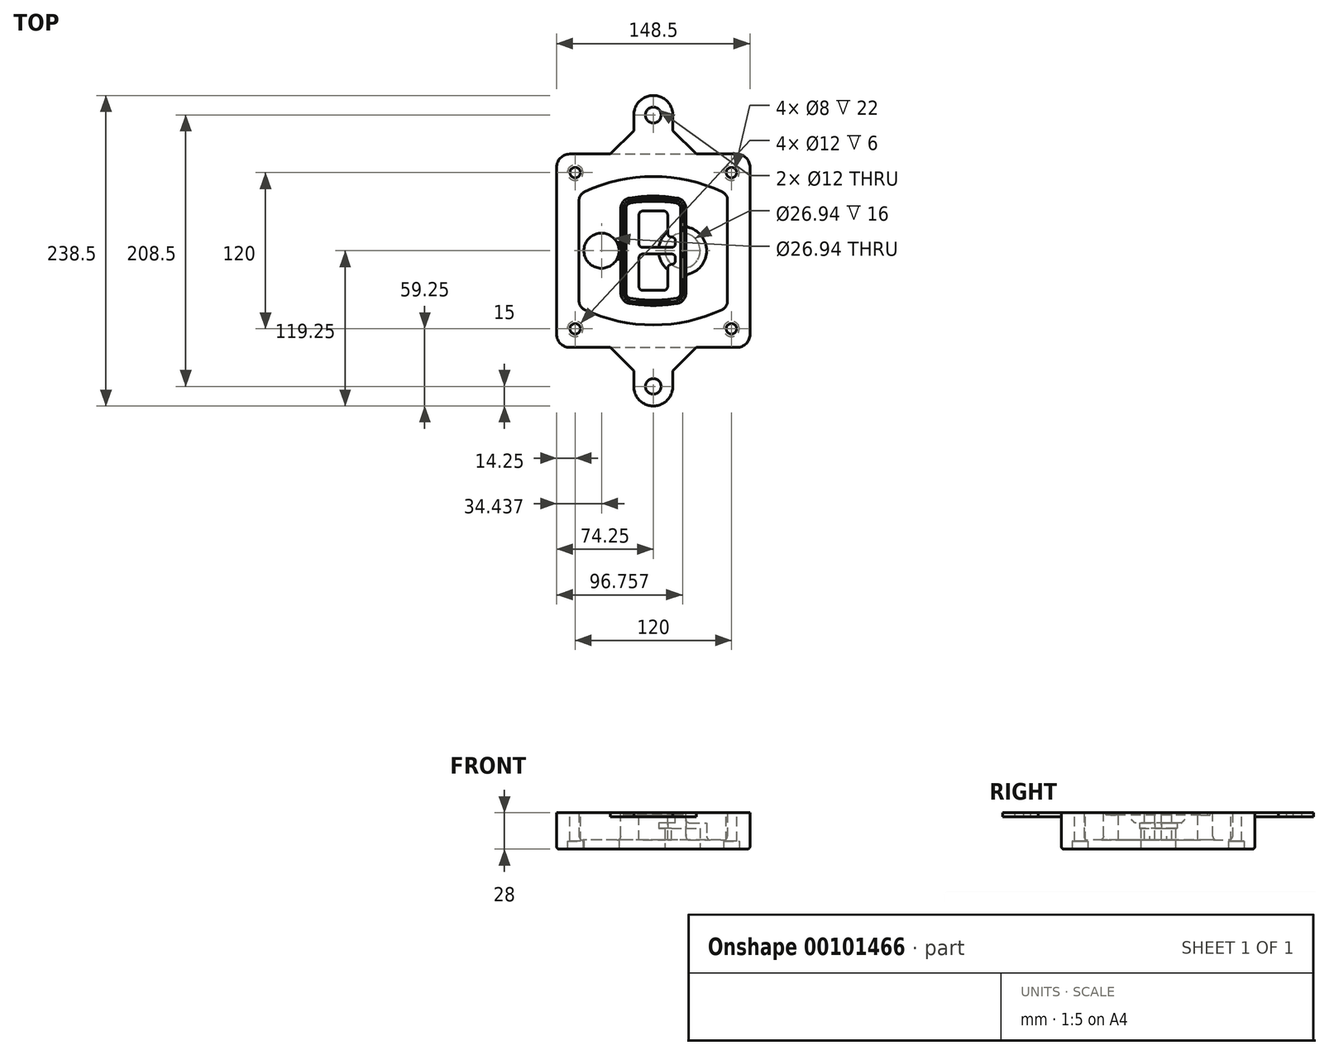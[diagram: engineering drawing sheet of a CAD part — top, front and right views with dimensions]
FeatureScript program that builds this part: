
annotation { "Feature Type Name" : "Feature", "Feature Type Description" : "" }
export const myFeature = defineFeature(function(context is Context, id is Id, definition is map)
    precondition{}
    {
        {
            var Q0;
            Q0=qCreatedBy(makeId("Top.planeOp"),FACE);
            var sketch = newSketch(context, id + "F0", { "sketchPlane" : qUnion([Q0])});
            skPoint(sketch, "E0.rect.middle", {"position": v(0, 0) * mm});
            skLineSegment(sketch, "E1.bottom", {"start": v(-64.25, -74.25) * mm, "end": v(64.25, -74.25) * mm});
            skLineSegment(sketch, "E1.top", {"start": v(-64.25, 74.25) * mm, "end": v(64.25, 74.25) * mm});
            skLineSegment(sketch, "E1.left", {"start": v(-74.25, -64.25) * mm, "end": v(-74.25, 64.25) * mm});
            skLineSegment(sketch, "E1.right", {"start": v(74.25, -64.25) * mm, "end": v(74.25, 64.25) * mm});
            skLineSegment(sketch, "E2", {"start": v(-74.25, 74.25) * mm, "end": v(74.25, -74.25) * mm, "construction": true});
            skLineSegment(sketch, "E3", {"start": v(74.25, 74.25) * mm, "end": v(-74.25, -74.25) * mm, "construction": true});
            skCircle(sketch, "E4", {"center": v(-60, 60) * mm, "radius": 4 * mm});
            skCircle(sketch, "E5", {"center": v(60, 60) * mm, "radius": 4 * mm});
            skCircle(sketch, "E6", {"center": v(60, -60) * mm, "radius": 4 * mm});
            skCircle(sketch, "E7", {"center": v(-60, -60) * mm, "radius": 4 * mm});
            skLineSegment(sketch, "E8", {"start": v(-60, 60) * mm, "end": v(60, 60) * mm, "construction": true});
            skLineSegment(sketch, "E9", {"start": v(60, 60) * mm, "end": v(60, -60) * mm, "construction": true});
            skLineSegment(sketch, "E10", {"start": v(60, -60) * mm, "end": v(-60, -60) * mm, "construction": true});
            skLineSegment(sketch, "E11", {"start": v(-60, -60) * mm, "end": v(-60, 60) * mm, "construction": true});
            skLineSegment(sketch, "E12", {"start": v(-60, 38.83) * mm, "end": v(-60, -38.83) * mm});
            skLineSegment(sketch, "E13", {"start": v(60, 38.83) * mm, "end": v(60, -38.83) * mm});
            skArc(sketch, "E14", {"start": v(54.26, 47.88) * mm, "mid": v(0, 60) * mm, "end": v(-54.26, 47.88) * mm});
            skArc(sketch, "E15", {"start": v(-54.26, -47.88) * mm, "mid": v(0, -60) * mm, "end": v(54.26, -47.88) * mm});
            skLineSegment(sketch, "E16", {"start": v(-60, 0) * mm, "end": v(60, 0) * mm, "construction": true});
            skPoint(sketch, "E17.visualSharp", {"position": v(-60, -45) * mm});
            skArc(sketch, "E17.filletArc", {"start": v(-60, -38.83) * mm, "mid": v(-58.44, -44.2) * mm, "end": v(-54.26, -47.88) * mm});
            skPoint(sketch, "E18.visualSharp", {"position": v(-60, 45) * mm});
            skArc(sketch, "E18.filletArc", {"start": v(-54.26, 47.88) * mm, "mid": v(-58.44, 44.2) * mm, "end": v(-60, 38.83) * mm});
            skPoint(sketch, "E19.visualSharp", {"position": v(60, 45) * mm});
            skArc(sketch, "E19.filletArc", {"start": v(60, 38.83) * mm, "mid": v(58.44, 44.2) * mm, "end": v(54.26, 47.88) * mm});
            skPoint(sketch, "E20.visualSharp", {"position": v(60, -45) * mm});
            skArc(sketch, "E20.filletArc", {"start": v(54.26, -47.88) * mm, "mid": v(58.44, -44.2) * mm, "end": v(60, -38.83) * mm});
            skPoint(sketch, "E21.visualSharp", {"position": v(-74.25, 74.25) * mm});
            skArc(sketch, "E21.filletArc", {"start": v(-64.25, 74.25) * mm, "mid": v(-71.32, 71.32) * mm, "end": v(-74.25, 64.25) * mm});
            skPoint(sketch, "E22.visualSharp", {"position": v(74.25, 74.25) * mm});
            skArc(sketch, "E22.filletArc", {"start": v(74.25, 64.25) * mm, "mid": v(71.32, 71.32) * mm, "end": v(64.25, 74.25) * mm});
            skPoint(sketch, "E23.visualSharp", {"position": v(74.25, -74.25) * mm});
            skArc(sketch, "E23.filletArc", {"start": v(64.25, -74.25) * mm, "mid": v(71.32, -71.32) * mm, "end": v(74.25, -64.25) * mm});
            skPoint(sketch, "E24.visualSharp", {"position": v(-74.25, -74.25) * mm});
            skArc(sketch, "E24.filletArc", {"start": v(-74.25, -64.25) * mm, "mid": v(-71.32, -71.32) * mm, "end": v(-64.25, -74.25) * mm});
            skArc(sketch, "E25.0", {"start": v(57, 38.83) * mm, "mid": v(55.9, 42.58) * mm, "end": v(52.98, 45.17) * mm});
            skLineSegment(sketch, "E25.1", {"start": v(57, 38.83) * mm, "end": v(57, -38.83) * mm});
            skArc(sketch, "E25.2", {"start": v(52.98, -45.17) * mm, "mid": v(55.9, -42.58) * mm, "end": v(57, -38.83) * mm});
            skArc(sketch, "E25.3", {"start": v(-52.98, -45.17) * mm, "mid": v(0, -57) * mm, "end": v(52.98, -45.17) * mm});
            skArc(sketch, "E25.4", {"start": v(-57, -38.83) * mm, "mid": v(-55.9, -42.58) * mm, "end": v(-52.98, -45.17) * mm});
            skArc(sketch, "E25.5", {"start": v(52.98, 45.17) * mm, "mid": v(0, 57) * mm, "end": v(-52.98, 45.17) * mm});
            skLineSegment(sketch, "E25.6", {"start": v(-57, 38.83) * mm, "end": v(-57, -38.83) * mm});
            skArc(sketch, "E25.7", {"start": v(-52.98, 45.17) * mm, "mid": v(-55.9, 42.58) * mm, "end": v(-57, 38.83) * mm});
            skArc(sketch, "E26.0", {"start": v(-55.96, 51.5) * mm, "mid": v(-61.82, 46.33) * mm, "end": v(-64, 38.83) * mm});
            skArc(sketch, "E26.1", {"start": v(55.96, 51.5) * mm, "mid": v(0, 64) * mm, "end": v(-55.96, 51.5) * mm});
            skArc(sketch, "E26.2", {"start": v(64, 38.83) * mm, "mid": v(61.82, 46.33) * mm, "end": v(55.96, 51.5) * mm});
            skLineSegment(sketch, "E26.3", {"start": v(64, 38.83) * mm, "end": v(64, -38.83) * mm});
            skArc(sketch, "E26.4", {"start": v(55.96, -51.5) * mm, "mid": v(61.82, -46.33) * mm, "end": v(64, -38.83) * mm});
            skLineSegment(sketch, "E26.5", {"start": v(-64, 38.83) * mm, "end": v(-64, -38.83) * mm});
            skArc(sketch, "E26.6", {"start": v(-55.96, -51.5) * mm, "mid": v(0, -64) * mm, "end": v(55.96, -51.5) * mm});
            skArc(sketch, "E26.7", {"start": v(-64, -38.83) * mm, "mid": v(-61.82, -46.33) * mm, "end": v(-55.96, -51.5) * mm});
            skSolve(sketch);
        }
        {
            var Q0;
            Q0=makeQuery(id+"F0.imprint","IMPRINT",FACE,{"disambiguationData":[TD([[makeQuery(id+"F0.imprint","IMPRINT",EDGE,{"derivedFrom":sQuery(id+"F0.wireOp",EDGE,"E1.bottom")}),1.0]])]});
            var Q1;
            Q1=makeQuery(id+"F0.imprint","IMPRINT",FACE,{"disambiguationData":[TD([[makeQuery(id+"F0.imprint","IMPRINT",EDGE,{"derivedFrom":sQuery(id+"F0.wireOp",EDGE,"E12")}),1.0]])]});
            var Q2;
            Q2=makeQuery(id+"F0.imprint","IMPRINT",FACE,{"disambiguationData":[TD([[makeQuery(id+"F0.imprint","IMPRINT",EDGE,{"derivedFrom":sQuery(id+"F0.wireOp",EDGE,"E25.0")}),1.0]])]});
            var Q3;
            Q3=makeQuery(id+"F0.imprint","IMPRINT",FACE,{"disambiguationData":[TD([[makeQuery(id+"F0.imprint","IMPRINT",EDGE,{"derivedFrom":sQuery(id+"F0.wireOp",EDGE,"E12")}),-1.0]])]});
            extrude(context, id + "F1", {"entities" : qUnion([Q0, Q1, Q2, Q3]), "oppositeDirection" : true, "depth" : 25 * mm});
        }
        {
            var Q0;
            Q0=makeQuery(id+"F0.imprint","IMPRINT",FACE,{"disambiguationData":[TD([[makeQuery(id+"F0.imprint","IMPRINT",EDGE,{"derivedFrom":sQuery(id+"F0.wireOp",EDGE,"E12")}),1.0]])]});
            extrude(context, id + "F2", {"entities" : qUnion([Q0]), "operationType" : NewBodyOperationType.ADD, "depth" : 3 * mm});
        }
        {
            var Q0;
            Q0=makeQuery(id+"F0.imprint","IMPRINT",FACE,{"disambiguationData":[TD([[makeQuery(id+"F0.imprint","IMPRINT",EDGE,{"derivedFrom":sQuery(id+"F0.wireOp",EDGE,"E25.0")}),1.0]])]});
            extrude(context, id + "F3", {"entities" : qUnion([Q0]), "operationType" : NewBodyOperationType.REMOVE, "oppositeDirection" : true, "depth" : 18 * mm});
        }
        {
            var Q0;
            Q0=makeQuery(id+"F2.opExtrude","CAP_FACE",FACE,{"disambiguationData":[OSD([sQuery(id+"F0.wireOp",EDGE,"E12"),sQuery(id+"F0.wireOp",EDGE,"E13"),sQuery(id+"F0.wireOp",EDGE,"E14"),sQuery(id+"F0.wireOp",EDGE,"E15"),sQuery(id+"F0.wireOp",EDGE,"E17.filletArc"),sQuery(id+"F0.wireOp",EDGE,"E18.filletArc"),sQuery(id+"F0.wireOp",EDGE,"E19.filletArc"),sQuery(id+"F0.wireOp",EDGE,"E20.filletArc"),sQuery(id+"F0.wireOp",EDGE,"E25.0"),sQuery(id+"F0.wireOp",EDGE,"E25.1"),sQuery(id+"F0.wireOp",EDGE,"E25.2"),sQuery(id+"F0.wireOp",EDGE,"E25.3"),sQuery(id+"F0.wireOp",EDGE,"E25.4"),sQuery(id+"F0.wireOp",EDGE,"E25.5"),sQuery(id+"F0.wireOp",EDGE,"E25.6"),sQuery(id+"F0.wireOp",EDGE,"E25.7")])],"isStart":false});
            var sketch = newSketch(context, id + "F4", { "sketchPlane" : qUnion([Q0])});
            skArc(sketch, "E27.0", {"start": v(-18.34, -40.45) * mm, "mid": v(0, -42) * mm, "end": v(18.34, -40.45) * mm});
            skArc(sketch, "E28.0", {"start": v(18.34, 40.45) * mm, "mid": v(0, 42) * mm, "end": v(-18.34, 40.45) * mm});
            skLineSegment(sketch, "E29", {"start": v(-25, 32.57) * mm, "end": v(-25, -32.57) * mm});
            skLineSegment(sketch, "E30", {"start": v(25, 32.57) * mm, "end": v(25, -32.57) * mm});
            skLineSegment(sketch, "E31", {"start": v(-25, 39.1) * mm, "end": v(25, 39.1) * mm, "construction": true});
            skLineSegment(sketch, "E32", {"start": v(-25, -39.1) * mm, "end": v(25, -39.1) * mm, "construction": true});
            skPoint(sketch, "E33.visualSharp", {"position": v(-25, 39.1) * mm});
            skArc(sketch, "E33.filletArc", {"start": v(-18.34, 40.45) * mm, "mid": v(-23.11, 37.73) * mm, "end": v(-25, 32.57) * mm});
            skPoint(sketch, "E34.visualSharp", {"position": v(25, 39.1) * mm});
            skArc(sketch, "E34.filletArc", {"start": v(25, 32.57) * mm, "mid": v(23.11, 37.73) * mm, "end": v(18.34, 40.45) * mm});
            skPoint(sketch, "E35.visualSharp", {"position": v(25, -39.1) * mm});
            skArc(sketch, "E35.filletArc", {"start": v(18.34, -40.45) * mm, "mid": v(23.11, -37.73) * mm, "end": v(25, -32.57) * mm});
            skPoint(sketch, "E36.visualSharp", {"position": v(-25, -39.1) * mm});
            skArc(sketch, "E36.filletArc", {"start": v(-25, -32.57) * mm, "mid": v(-23.11, -37.73) * mm, "end": v(-18.34, -40.45) * mm});
            skArc(sketch, "E37.0", {"start": v(52.98, 45.17) * mm, "mid": v(0, 57) * mm, "end": v(-52.98, 45.17) * mm});
            skArc(sketch, "E37.1", {"start": v(-52.98, 45.17) * mm, "mid": v(-55.9, 42.58) * mm, "end": v(-57, 38.83) * mm});
            skLineSegment(sketch, "E37.2", {"start": v(-57, 38.83) * mm, "end": v(-57, -38.83) * mm});
            skArc(sketch, "E37.3", {"start": v(-57, -38.83) * mm, "mid": v(-55.9, -42.58) * mm, "end": v(-52.98, -45.17) * mm});
            skArc(sketch, "E37.4", {"start": v(-52.98, -45.17) * mm, "mid": v(0, -57) * mm, "end": v(52.98, -45.17) * mm});
            skArc(sketch, "E37.5", {"start": v(52.98, -45.17) * mm, "mid": v(55.9, -42.58) * mm, "end": v(57, -38.83) * mm});
            skLineSegment(sketch, "E37.6", {"start": v(57, 38.83) * mm, "end": v(57, -38.83) * mm});
            skArc(sketch, "E37.7", {"start": v(57, 38.83) * mm, "mid": v(55.9, 42.58) * mm, "end": v(52.98, 45.17) * mm});
            skLineSegment(sketch, "E38.0", {"start": v(23, 32.57) * mm, "end": v(23, -32.57) * mm});
            skArc(sketch, "E38.1", {"start": v(18, -38.48) * mm, "mid": v(21.58, -36.44) * mm, "end": v(23, -32.57) * mm});
            skArc(sketch, "E38.2", {"start": v(-18, -38.48) * mm, "mid": v(0, -40) * mm, "end": v(18, -38.48) * mm});
            skArc(sketch, "E38.3", {"start": v(-23, -32.57) * mm, "mid": v(-21.58, -36.44) * mm, "end": v(-18, -38.48) * mm});
            skLineSegment(sketch, "E38.4", {"start": v(-23, 32.57) * mm, "end": v(-23, -32.57) * mm});
            skArc(sketch, "E38.5", {"start": v(23, 32.57) * mm, "mid": v(21.58, 36.44) * mm, "end": v(18, 38.48) * mm});
            skArc(sketch, "E38.6", {"start": v(-18, 38.48) * mm, "mid": v(-21.58, 36.44) * mm, "end": v(-23, 32.57) * mm});
            skArc(sketch, "E38.7", {"start": v(18, 38.48) * mm, "mid": v(0, 40) * mm, "end": v(-18, 38.48) * mm});
            skArc(sketch, "E39.0", {"start": v(21, 32.57) * mm, "mid": v(20.06, 35.15) * mm, "end": v(17.67, 36.5) * mm});
            skLineSegment(sketch, "E39.1", {"start": v(21, 32.57) * mm, "end": v(21, -32.57) * mm});
            skArc(sketch, "E39.2", {"start": v(17.67, -36.5) * mm, "mid": v(20.06, -35.15) * mm, "end": v(21, -32.57) * mm});
            skArc(sketch, "E39.3", {"start": v(-17.67, -36.5) * mm, "mid": v(0, -38) * mm, "end": v(17.67, -36.5) * mm});
            skArc(sketch, "E39.4", {"start": v(-21, -32.57) * mm, "mid": v(-20.06, -35.15) * mm, "end": v(-17.67, -36.5) * mm});
            skArc(sketch, "E39.5", {"start": v(17.67, 36.5) * mm, "mid": v(0, 38) * mm, "end": v(-17.67, 36.5) * mm});
            skLineSegment(sketch, "E39.6", {"start": v(-21, 32.57) * mm, "end": v(-21, -32.57) * mm});
            skArc(sketch, "E39.7", {"start": v(-17.67, 36.5) * mm, "mid": v(-20.06, 35.15) * mm, "end": v(-21, 32.57) * mm});
            skLineSegment(sketch, "E40", {"start": v(-25, 0) * mm, "end": v(25, 0) * mm, "construction": true});
            skLineSegment(sketch, "E41", {"start": v(-11, 5.5) * mm, "end": v(-11, 27.5) * mm});
            skLineSegment(sketch, "E42", {"start": v(-8, 30.5) * mm, "end": v(8, 30.5) * mm});
            skLineSegment(sketch, "E43", {"start": v(11, 27.5) * mm, "end": v(11, 13.5) * mm});
            skLineSegment(sketch, "E44", {"start": v(14, 10.5) * mm, "end": v(14, 10.5) * mm});
            skLineSegment(sketch, "E45", {"start": v(17, 7.5) * mm, "end": v(17, 5.5) * mm});
            skLineSegment(sketch, "E46", {"start": v(14, 2.5) * mm, "end": v(-8, 2.5) * mm});
            skPoint(sketch, "E47.visualSharp", {"position": v(-11, 30.5) * mm});
            skArc(sketch, "E47.filletArc", {"start": v(-8, 30.5) * mm, "mid": v(-10.12, 29.62) * mm, "end": v(-11, 27.5) * mm});
            skPoint(sketch, "E48.visualSharp", {"position": v(11, 30.5) * mm});
            skArc(sketch, "E48.filletArc", {"start": v(11, 27.5) * mm, "mid": v(10.12, 29.62) * mm, "end": v(8, 30.5) * mm});
            skPoint(sketch, "E49.visualSharp", {"position": v(11, 10.5) * mm});
            skArc(sketch, "E49.filletArc", {"start": v(11, 13.5) * mm, "mid": v(11.88, 11.38) * mm, "end": v(14, 10.5) * mm});
            skPoint(sketch, "E50.visualSharp", {"position": v(17, 10.5) * mm});
            skArc(sketch, "E50.filletArc", {"start": v(17, 7.5) * mm, "mid": v(16.12, 9.62) * mm, "end": v(14, 10.5) * mm});
            skPoint(sketch, "E51.visualSharp", {"position": v(17, 2.5) * mm});
            skArc(sketch, "E51.filletArc", {"start": v(14, 2.5) * mm, "mid": v(16.12, 3.38) * mm, "end": v(17, 5.5) * mm});
            skPoint(sketch, "E52.visualSharp", {"position": v(-11, 2.5) * mm});
            skArc(sketch, "E52.filletArc", {"start": v(-11, 5.5) * mm, "mid": v(-10.12, 3.38) * mm, "end": v(-8, 2.5) * mm});
            skLineSegment(sketch, "E53.0.MirrorCS", {"start": v(14, -2.5) * mm, "end": v(-8, -2.5) * mm});
            skArc(sketch, "E54.0.MirrorCS", {"start": v(-11, -5.5) * mm, "mid": v(-10.12, -3.38) * mm, "end": v(-8, -2.5) * mm});
            skLineSegment(sketch, "E55.0.MirrorCS", {"start": v(-11, -5.5) * mm, "end": v(-11, -27.5) * mm});
            skArc(sketch, "E56.0.MirrorCS", {"start": v(-8, -30.5) * mm, "mid": v(-10.12, -29.62) * mm, "end": v(-11, -27.5) * mm});
            skLineSegment(sketch, "E57.0.MirrorCS", {"start": v(-8, -30.5) * mm, "end": v(8, -30.5) * mm});
            skArc(sketch, "E58.0.MirrorCS", {"start": v(11, -27.5) * mm, "mid": v(10.12, -29.62) * mm, "end": v(8, -30.5) * mm});
            skLineSegment(sketch, "E59.0.MirrorCS", {"start": v(11, -27.5) * mm, "end": v(11, -13.5) * mm});
            skArc(sketch, "E60.0.MirrorCS", {"start": v(11, -13.5) * mm, "mid": v(11.88, -11.38) * mm, "end": v(14, -10.5) * mm});
            skArc(sketch, "E61.0.MirrorCS", {"start": v(17, -7.5) * mm, "mid": v(16.12, -9.62) * mm, "end": v(14, -10.5) * mm});
            skLineSegment(sketch, "E62.0.MirrorCS", {"start": v(17, -7.5) * mm, "end": v(17, -5.5) * mm});
            skArc(sketch, "E63.0.MirrorCS", {"start": v(14, -2.5) * mm, "mid": v(16.12, -3.38) * mm, "end": v(17, -5.5) * mm});
            skSolve(sketch);
        }
        {
            var Q0;
            Q0=makeQuery(id+"F4.imprint","IMPRINT",FACE,{"disambiguationData":[TD([[makeQuery(id+"F4.imprint","IMPRINT",EDGE,{"derivedFrom":sQuery(id+"F4.wireOp",EDGE,"E27.0")}),1.0]])]});
            var Q1;
            Q1=makeQuery(id+"F4.imprint","IMPRINT",FACE,{"disambiguationData":[TD([[makeQuery(id+"F4.imprint","IMPRINT",EDGE,{"derivedFrom":sQuery(id+"F4.wireOp",EDGE,"E38.0")}),-1.0]])]});
            var Q2;
            Q2=makeQuery(id+"F4.imprint","IMPRINT",FACE,{"disambiguationData":[TD([[makeQuery(id+"F4.imprint","IMPRINT",EDGE,{"derivedFrom":sQuery(id+"F4.wireOp",EDGE,"E39.0")}),1.0]])]});
            extrude(context, id + "F5", {"entities" : qUnion([Q0, Q1, Q2]), "operationType" : NewBodyOperationType.ADD, "endBound" : BoundingType.UP_TO_NEXT, "oppositeDirection" : true, "depth" : 25 * mm});
        }
        {
            var Q0;
            Q0=makeQuery(id+"F4.imprint","IMPRINT",FACE,{"disambiguationData":[TD([[makeQuery(id+"F4.imprint","IMPRINT",EDGE,{"derivedFrom":sQuery(id+"F4.wireOp",EDGE,"E38.0")}),-1.0]])]});
            extrude(context, id + "F6", {"entities" : qUnion([Q0]), "operationType" : NewBodyOperationType.REMOVE, "oppositeDirection" : true, "depth" : 2 * mm});
        }
        {
            var Q0;
            Q0=makeQuery(id+"F1.opExtrude","CAP_FACE",FACE,{"disambiguationData":[OSD([sQuery(id+"F0.wireOp",EDGE,"E1.bottom"),sQuery(id+"F0.wireOp",EDGE,"E1.top"),sQuery(id+"F0.wireOp",EDGE,"E1.left"),sQuery(id+"F0.wireOp",EDGE,"E1.right"),sQuery(id+"F0.wireOp",EDGE,"E4"),sQuery(id+"F0.wireOp",EDGE,"E5"),sQuery(id+"F0.wireOp",EDGE,"E6"),sQuery(id+"F0.wireOp",EDGE,"E7"),sQuery(id+"F0.wireOp",EDGE,"E21.filletArc"),sQuery(id+"F0.wireOp",EDGE,"E22.filletArc"),sQuery(id+"F0.wireOp",EDGE,"E23.filletArc"),sQuery(id+"F0.wireOp",EDGE,"E24.filletArc")])],"isStart":false});
            var sketch = newSketch(context, id + "F7", { "sketchPlane" : qUnion([Q0])});
            skCircle(sketch, "E64", {"center": v(22.5, 0) * mm, "radius": 13.47 * mm});
            skCircle(sketch, "E65", {"center": v(-39.81, 0) * mm, "radius": 13.47 * mm});
            skLineSegment(sketch, "E66", {"start": v(74.25, 0) * mm, "end": v(-74.25, 0) * mm});
            skCircle(sketch, "E67", {"center": v(22.5, 0) * mm, "radius": 18.47 * mm});
            skCircle(sketch, "E68", {"center": v(60, -60) * mm, "radius": 6 * mm});
            skCircle(sketch, "E69", {"center": v(-60, -60) * mm, "radius": 6 * mm});
            skCircle(sketch, "E70", {"center": v(-60, 60) * mm, "radius": 6 * mm});
            skCircle(sketch, "E71", {"center": v(60, 60) * mm, "radius": 6 * mm});
            skSolve(sketch);
        }
        {
            var Q0;
            {var subQ1=sQuery(id+"F7.wireOp",EDGE,"E66");var subQ4=sQuery(id+"F7.wireOp",EDGE,"E64");var subQ6=makeQuery(id+"F7.imprint","INTERSECT",VERTEX,{"disambiguationData":[OD(0.0)],"derivedFrom":[subQ4,subQ1]});Q0=makeQuery(id+"F7.imprint","IMPRINT",FACE,{"disambiguationData":[TD([[makeQuery(id+"F7.imprint","IMPRINT",EDGE,{"disambiguationData":[TD([[subQ6,-1.0]])],"derivedFrom":subQ4}),-1.0]])]});}
            var Q1;
            {var subQ0=sQuery(id+"F7.wireOp",EDGE,"E66");var subQ1=sQuery(id+"F7.wireOp",EDGE,"E64");var subQ3=makeQuery(id+"F7.imprint","INTERSECT",VERTEX,{"disambiguationData":[OD(0.0)],"derivedFrom":[subQ1,subQ0]});Q1=makeQuery(id+"F7.imprint","IMPRINT",FACE,{"disambiguationData":[TD([[makeQuery(id+"F7.imprint","IMPRINT",EDGE,{"disambiguationData":[TD([[subQ3,-1.0]])],"derivedFrom":subQ1}),1.0]])]});}
            var Q2;
            {var subQ0=sQuery(id+"F7.wireOp",EDGE,"E66");var subQ1=sQuery(id+"F7.wireOp",EDGE,"E64");var subQ3=makeQuery(id+"F7.imprint","INTERSECT",VERTEX,{"disambiguationData":[OD(0.0)],"derivedFrom":[subQ1,subQ0]});Q2=makeQuery(id+"F7.imprint","IMPRINT",FACE,{"disambiguationData":[TD([[makeQuery(id+"F7.imprint","IMPRINT",EDGE,{"disambiguationData":[TD([[subQ3,1.0]])],"derivedFrom":subQ1}),1.0]])]});}
            var Q3;
            {var subQ1=sQuery(id+"F7.wireOp",EDGE,"E66");var subQ4=sQuery(id+"F7.wireOp",EDGE,"E64");var subQ6=makeQuery(id+"F7.imprint","INTERSECT",VERTEX,{"disambiguationData":[OD(0.0)],"derivedFrom":[subQ4,subQ1]});Q3=makeQuery(id+"F7.imprint","IMPRINT",FACE,{"disambiguationData":[TD([[makeQuery(id+"F7.imprint","IMPRINT",EDGE,{"disambiguationData":[TD([[subQ6,1.0]])],"derivedFrom":subQ4}),-1.0]])]});}
            extrude(context, id + "F8", {"entities" : qUnion([Q0, Q1, Q2, Q3]), "operationType" : NewBodyOperationType.ADD, "oppositeDirection" : true, "depth" : 20 * mm});
        }
        {
            var Q0;
            {var subQ0=sQuery(id+"F7.wireOp",EDGE,"E66");var subQ1=sQuery(id+"F7.wireOp",EDGE,"E64");var subQ3=makeQuery(id+"F7.imprint","INTERSECT",VERTEX,{"disambiguationData":[OD(0.0)],"derivedFrom":[subQ1,subQ0]});Q0=makeQuery(id+"F7.imprint","IMPRINT",FACE,{"disambiguationData":[TD([[makeQuery(id+"F7.imprint","IMPRINT",EDGE,{"disambiguationData":[TD([[subQ3,-1.0]])],"derivedFrom":subQ1}),1.0]])]});}
            var Q1;
            {var subQ0=sQuery(id+"F7.wireOp",EDGE,"E66");var subQ1=sQuery(id+"F7.wireOp",EDGE,"E64");var subQ3=makeQuery(id+"F7.imprint","INTERSECT",VERTEX,{"disambiguationData":[OD(0.0)],"derivedFrom":[subQ1,subQ0]});Q1=makeQuery(id+"F7.imprint","IMPRINT",FACE,{"disambiguationData":[TD([[makeQuery(id+"F7.imprint","IMPRINT",EDGE,{"disambiguationData":[TD([[subQ3,1.0]])],"derivedFrom":subQ1}),1.0]])]});}
            extrude(context, id + "F9", {"entities" : qUnion([Q0, Q1]), "operationType" : NewBodyOperationType.REMOVE, "oppositeDirection" : true, "depth" : 16 * mm});
        }
        {
            var Q0;
            {var subQ0=sQuery(id+"F7.wireOp",EDGE,"E66");var subQ1=sQuery(id+"F7.wireOp",EDGE,"E65");var subQ3=makeQuery(id+"F7.imprint","INTERSECT",VERTEX,{"disambiguationData":[OD(0.0)],"derivedFrom":[subQ1,subQ0]});Q0=makeQuery(id+"F7.imprint","IMPRINT",FACE,{"disambiguationData":[TD([[makeQuery(id+"F7.imprint","IMPRINT",EDGE,{"disambiguationData":[TD([[subQ3,-1.0]])],"derivedFrom":subQ1}),1.0]])]});}
            var Q1;
            {var subQ0=sQuery(id+"F7.wireOp",EDGE,"E66");var subQ1=sQuery(id+"F7.wireOp",EDGE,"E65");var subQ3=makeQuery(id+"F7.imprint","INTERSECT",VERTEX,{"disambiguationData":[OD(0.0)],"derivedFrom":[subQ1,subQ0]});Q1=makeQuery(id+"F7.imprint","IMPRINT",FACE,{"disambiguationData":[TD([[makeQuery(id+"F7.imprint","IMPRINT",EDGE,{"disambiguationData":[TD([[subQ3,1.0]])],"derivedFrom":subQ1}),1.0]])]});}
            extrude(context, id + "F10", {"entities" : qUnion([Q0, Q1]), "operationType" : NewBodyOperationType.REMOVE, "oppositeDirection" : true, "depth" : 25 * mm});
        }
        {
            var Q0;
            Q0=makeQuery(id+"F7.imprint","IMPRINT",FACE,{"disambiguationData":[TD([[makeQuery(id+"F7.imprint","IMPRINT",EDGE,{"derivedFrom":sQuery(id+"F7.wireOp",EDGE,"E68")}),1.0]])]});
            var Q1;
            Q1=makeQuery(id+"F7.imprint","IMPRINT",FACE,{"disambiguationData":[TD([[makeQuery(id+"F7.imprint","IMPRINT",EDGE,{"derivedFrom":makeQuery(id+"F1.opExtrude","CAP_EDGE",EDGE,{"disambiguationData":[OSD([sQuery(id+"F0.wireOp",EDGE,"E5")])],"isStart":false})}),-1.0]])]});
            var Q2;
            Q2=makeQuery(id+"F7.imprint","IMPRINT",FACE,{"disambiguationData":[TD([[makeQuery(id+"F7.imprint","IMPRINT",EDGE,{"derivedFrom":sQuery(id+"F7.wireOp",EDGE,"E69")}),1.0]])]});
            var Q3;
            Q3=makeQuery(id+"F7.imprint","IMPRINT",FACE,{"disambiguationData":[TD([[makeQuery(id+"F7.imprint","IMPRINT",EDGE,{"derivedFrom":makeQuery(id+"F1.opExtrude","CAP_EDGE",EDGE,{"disambiguationData":[OSD([sQuery(id+"F0.wireOp",EDGE,"E4")])],"isStart":false})}),-1.0]])]});
            var Q4;
            Q4=makeQuery(id+"F7.imprint","IMPRINT",FACE,{"disambiguationData":[TD([[makeQuery(id+"F7.imprint","IMPRINT",EDGE,{"derivedFrom":sQuery(id+"F7.wireOp",EDGE,"E70")}),1.0]])]});
            var Q5;
            Q5=makeQuery(id+"F7.imprint","IMPRINT",FACE,{"disambiguationData":[TD([[makeQuery(id+"F7.imprint","IMPRINT",EDGE,{"derivedFrom":makeQuery(id+"F1.opExtrude","CAP_EDGE",EDGE,{"disambiguationData":[OSD([sQuery(id+"F0.wireOp",EDGE,"E7")])],"isStart":false})}),-1.0]])]});
            var Q6;
            Q6=makeQuery(id+"F7.imprint","IMPRINT",FACE,{"disambiguationData":[TD([[makeQuery(id+"F7.imprint","IMPRINT",EDGE,{"derivedFrom":sQuery(id+"F7.wireOp",EDGE,"E71")}),1.0]])]});
            var Q7;
            Q7=makeQuery(id+"F7.imprint","IMPRINT",FACE,{"disambiguationData":[TD([[makeQuery(id+"F7.imprint","IMPRINT",EDGE,{"derivedFrom":makeQuery(id+"F1.opExtrude","CAP_EDGE",EDGE,{"disambiguationData":[OSD([sQuery(id+"F0.wireOp",EDGE,"E6")])],"isStart":false})}),-1.0]])]});
            extrude(context, id + "F11", {"entities" : qUnion([Q0, Q1, Q2, Q3, Q4, Q5, Q6, Q7]), "operationType" : NewBodyOperationType.REMOVE, "oppositeDirection" : true, "depth" : 6 * mm});
        }
        {
            var Q0;
            Q0=makeQuery(id+"F9.boolean.opBoolean","COPY",FACE,{"derivedFrom":makeQuery(id+"F9.opExtrude","CAP_FACE",FACE,{"disambiguationData":[OSD([sQuery(id+"F7.wireOp",EDGE,"E64")])],"isStart":false})});
            var sketch = newSketch(context, id + "F12", { "sketchPlane" : qUnion([Q0])});
            skArc(sketch, "E72.0", {"start": v(11, 14.45) * mm, "mid": v(6.45, 9.13) * mm, "end": v(4.2, 2.5) * mm});
            skArc(sketch, "E72.1", {"start": v(4.2, -2.5) * mm, "mid": v(6.45, -9.13) * mm, "end": v(11, -14.45) * mm});
            skLineSegment(sketch, "E73", {"start": v(4.2, -2.5) * mm, "end": v(14, -2.5) * mm});
            skLineSegment(sketch, "E74.0", {"start": v(14, 2.5) * mm, "end": v(4.2, 2.5) * mm});
            skArc(sketch, "E74.1", {"start": v(14, 2.5) * mm, "mid": v(16.12, 3.38) * mm, "end": v(17, 5.5) * mm});
            skLineSegment(sketch, "E74.2", {"start": v(17, 7.5) * mm, "end": v(17, 5.5) * mm});
            skArc(sketch, "E74.3", {"start": v(17, 7.5) * mm, "mid": v(16.12, 9.62) * mm, "end": v(14, 10.5) * mm});
            skArc(sketch, "E74.4", {"start": v(11, 13.5) * mm, "mid": v(11.88, 11.38) * mm, "end": v(14, 10.5) * mm});
            skLineSegment(sketch, "E74.5", {"start": v(11, 14.45) * mm, "end": v(11, 13.5) * mm});
            skLineSegment(sketch, "E74.7", {"start": v(14, -2.5) * mm, "end": v(4.2, -2.5) * mm});
            skArc(sketch, "E74.8", {"start": v(14, -2.5) * mm, "mid": v(16.12, -3.38) * mm, "end": v(17, -5.5) * mm});
            skLineSegment(sketch, "E74.9", {"start": v(17, -7.5) * mm, "end": v(17, -5.5) * mm});
            skArc(sketch, "E74.10", {"start": v(17, -7.5) * mm, "mid": v(16.12, -9.62) * mm, "end": v(14, -10.5) * mm});
            skArc(sketch, "E74.11", {"start": v(11, -13.5) * mm, "mid": v(11.88, -11.38) * mm, "end": v(14, -10.5) * mm});
            skLineSegment(sketch, "E74.12", {"start": v(11, -14.45) * mm, "end": v(11, -13.5) * mm});
            skPoint(sketch, "E75.orphan", {"position": v(11, -27.5) * mm});
            skPoint(sketch, "E76.orphan", {"position": v(-8, -2.5) * mm});
            skPoint(sketch, "E77.orphan", {"position": v(-8, 2.5) * mm});
            skPoint(sketch, "E78.orphan", {"position": v(11, 27.5) * mm});
            skSolve(sketch);
        }
        {
            var Q0;
            {var subQ7=sQuery(id+"F12.wireOp",EDGE,"E72.0");var subQ14=sQuery(id+"F12.wireOp",EDGE,"E72.1");var subQ16=sQuery(id+"F12.wireOp",EDGE,"E74.1");var subQ18=sQuery(id+"F12.wireOp",EDGE,"E74.8");Q0=qUnion([makeQuery(id+"F12.imprint","IMPRINT",FACE,{"disambiguationData":[TD([[makeQuery(id+"F12.imprint","IMPRINT",EDGE,{"derivedFrom":subQ7}),1.0]])]}),makeQuery(id+"F12.imprint","IMPRINT",FACE,{"disambiguationData":[TD([[makeQuery(id+"F12.imprint","IMPRINT",EDGE,{"derivedFrom":subQ14}),1.0]])]}),makeQuery(id+"F12.imprint","IMPRINT",FACE,{"disambiguationData":[TD([[makeQuery(id+"F12.imprint","IMPRINT",EDGE,{"derivedFrom":subQ16}),1.0]])]}),makeQuery(id+"F12.imprint","IMPRINT",FACE,{"disambiguationData":[TD([[makeQuery(id+"F12.imprint","IMPRINT",EDGE,{"derivedFrom":subQ18}),-1.0]])]})]);}
            var Q1;
            Q1=makeQuery(id+"F5.boolean.opBoolean","SPLIT",FACE,{"disambiguationData":[TD([makeQuery(id+"F5.opExtrude","SWEPT_FACE",FACE,{"disambiguationData":[OSD([sQuery(id+"F4.wireOp",EDGE,"E41")])]})])],"derivedFrom":makeQuery(id+"F3.boolean.opBoolean","COPY",FACE,{"derivedFrom":makeQuery(id+"F3.opExtrude","CAP_FACE",FACE,{"disambiguationData":[OSD([sQuery(id+"F0.wireOp",EDGE,"E25.0"),sQuery(id+"F0.wireOp",EDGE,"E25.1"),sQuery(id+"F0.wireOp",EDGE,"E25.2"),sQuery(id+"F0.wireOp",EDGE,"E25.3"),sQuery(id+"F0.wireOp",EDGE,"E25.4"),sQuery(id+"F0.wireOp",EDGE,"E25.5"),sQuery(id+"F0.wireOp",EDGE,"E25.6"),sQuery(id+"F0.wireOp",EDGE,"E25.7")])],"isStart":false})})});
            extrude(context, id + "F13", {"entities" : qUnion([Q0]), "operationType" : NewBodyOperationType.REMOVE, "endBound" : BoundingType.UP_TO_SURFACE, "endBoundEntityFace" : qUnion([Q1]), "depth" : 25 * mm});
        }
        {
            var Q0;
            Q0=makeQuery(id+"F3.boolean.opBoolean","COPY",EDGE,{"derivedFrom":makeQuery(id+"F3.opExtrude","CAP_EDGE",EDGE,{"disambiguationData":[OSD([sQuery(id+"F0.wireOp",EDGE,"E25.6")])],"isStart":false})});
            var Q1;
            Q1=makeQuery(id+"F8.boolean.opBoolean","INTERSECT",EDGE,{"derivedFrom":[makeQuery(id+"F5.opExtrude","SWEPT_FACE",FACE,{"disambiguationData":[OSD([sQuery(id+"F4.wireOp",EDGE,"E30")])]}),makeQuery(id+"F8.opExtrude","CAP_FACE",FACE,{"disambiguationData":[OSD([sQuery(id+"F7.wireOp",EDGE,"E67")])],"isStart":false})]});
            var Q2;
            Q2=makeQuery(id+"F8.boolean.opBoolean","INTERSECT",EDGE,{"disambiguationData":[OD(1.0)],"derivedFrom":[makeQuery(id+"F5.opExtrude","SWEPT_FACE",FACE,{"disambiguationData":[OSD([sQuery(id+"F4.wireOp",EDGE,"E30")])]}),makeQuery(id+"F8.opExtrude","SWEPT_FACE",FACE,{"disambiguationData":[OSD([sQuery(id+"F7.wireOp",EDGE,"E67")])]})]});
            var Q3;
            {var subQ0=sQuery(id+"F4.wireOp",EDGE,"E30");Q3=makeQuery(id+"F8.boolean.opBoolean","SPLIT",EDGE,{"disambiguationData":[TD([makeQuery(id+"F5.opExtrude","SWEPT_FACE",FACE,{"disambiguationData":[OSD([sQuery(id+"F4.wireOp",EDGE,"E35.filletArc")])]})])],"derivedFrom":makeQuery(id+"F5.opExtrude","CAP_EDGE",EDGE,{"disambiguationData":[OSD([subQ0])],"isStart":false})});}
            var Q4;
            {var subQ0=sQuery(id+"F0.wireOp",EDGE,"E25.7");var subQ1=sQuery(id+"F0.wireOp",EDGE,"E25.1");var subQ2=sQuery(id+"F0.wireOp",EDGE,"E25.6");var subQ3=sQuery(id+"F0.wireOp",EDGE,"E25.5");var subQ4=sQuery(id+"F0.wireOp",EDGE,"E25.4");var subQ5=sQuery(id+"F0.wireOp",EDGE,"E25.0");var subQ6=sQuery(id+"F0.wireOp",EDGE,"E25.2");var subQ7=sQuery(id+"F0.wireOp",EDGE,"E25.3");Q4=makeQuery(id+"F8.boolean.opBoolean","INTERSECT",EDGE,{"derivedFrom":[makeQuery(id+"F5.boolean.opBoolean","SPLIT",FACE,{"disambiguationData":[TD([makeQuery(id+"F2.opExtrude","SWEPT_FACE",FACE,{"disambiguationData":[OSD([subQ5])]})])],"derivedFrom":makeQuery(id+"F3.boolean.opBoolean","COPY",FACE,{"derivedFrom":makeQuery(id+"F3.opExtrude","CAP_FACE",FACE,{"disambiguationData":[OSD([subQ5,subQ1,subQ6,subQ7,subQ4,subQ3,subQ2,subQ0])],"isStart":false})})}),makeQuery(id+"F8.opExtrude","SWEPT_FACE",FACE,{"disambiguationData":[OSD([sQuery(id+"F7.wireOp",EDGE,"E67")])]})]});}
            var Q5;
            Q5=makeQuery(id+"F8.boolean.opBoolean","INTERSECT",EDGE,{"disambiguationData":[OD(0.0)],"derivedFrom":[makeQuery(id+"F5.opExtrude","SWEPT_FACE",FACE,{"disambiguationData":[OSD([sQuery(id+"F4.wireOp",EDGE,"E30")])]}),makeQuery(id+"F8.opExtrude","SWEPT_FACE",FACE,{"disambiguationData":[OSD([sQuery(id+"F7.wireOp",EDGE,"E67")])]})]});
            fillet(context, id + "F14", {"entities" : qUnion([Q0, Q1, Q2, Q3, Q4, Q5]), "radius" : 3 * mm, "tangentPropagation" : true, "allowEdgeOverflow" : false});
        }
        {
            var Q0;
            Q0=makeQuery(id+"F1.opExtrude","CAP_EDGE",EDGE,{"disambiguationData":[OSD([sQuery(id+"F0.wireOp",EDGE,"E1.bottom")])],"isStart":false});
            fillet(context, id + "F15", {"entities" : qUnion([Q0]), "radius" : 2 * mm, "tangentPropagation" : true, "allowEdgeOverflow" : false});
        }
        {
            var Q0;
            {var subQ0=sQuery(id+"F0.wireOp",EDGE,"E22.filletArc");var subQ1=sQuery(id+"F0.wireOp",EDGE,"E7");var subQ2=sQuery(id+"F0.wireOp",EDGE,"E6");var subQ3=sQuery(id+"F0.wireOp",EDGE,"E5");var subQ4=sQuery(id+"F0.wireOp",EDGE,"E4");var subQ5=sQuery(id+"F0.wireOp",EDGE,"E1.bottom");var subQ6=sQuery(id+"F0.wireOp",EDGE,"E21.filletArc");var subQ7=sQuery(id+"F0.wireOp",EDGE,"E1.top");var subQ8=sQuery(id+"F0.wireOp",EDGE,"E1.left");var subQ9=sQuery(id+"F0.wireOp",EDGE,"E1.right");var subQ10=sQuery(id+"F0.wireOp",EDGE,"E23.filletArc");var subQ11=sQuery(id+"F0.wireOp",EDGE,"E24.filletArc");Q0=makeQuery(id+"F2.boolean.opBoolean","SPLIT",FACE,{"disambiguationData":[TD([makeQuery(id+"F1.opExtrude","SWEPT_FACE",FACE,{"disambiguationData":[OSD([subQ5])]})])],"derivedFrom":makeQuery(id+"F1.opExtrude","CAP_FACE",FACE,{"disambiguationData":[OSD([subQ5,subQ7,subQ8,subQ9,subQ4,subQ3,subQ2,subQ1,subQ6,subQ0,subQ10,subQ11])],"isStart":true})});}
            var sketch = newSketch(context, id + "F16", { "sketchPlane" : qUnion([Q0])});
            skLineSegment(sketch, "E79", {"start": v(0, 74.25) * mm, "end": v(0, 104.25) * mm, "construction": true});
            skLineSegment(sketch, "E80", {"start": v(-32.98, 74.25) * mm, "end": v(-14.98, 92.25) * mm});
            skLineSegment(sketch, "E81", {"start": v(-14.98, 92.25) * mm, "end": v(-14.98, 103.41) * mm});
            skArc(sketch, "E82", {"start": v(15, 104.25) * mm, "mid": v(-0.42, 119.24) * mm, "end": v(-14.98, 103.41) * mm});
            skLineSegment(sketch, "E83", {"start": v(15, 104.25) * mm, "end": v(15, 92.25) * mm});
            skLineSegment(sketch, "E84", {"start": v(15, 92.25) * mm, "end": v(33, 74.25) * mm});
            skCircle(sketch, "E85", {"center": v(0, 104.25) * mm, "radius": 6 * mm});
            skLineSegment(sketch, "E86", {"start": v(-74.25, 0) * mm, "end": v(74.25, 0) * mm, "construction": true});
            skLineSegment(sketch, "E87.MirrorCS", {"start": v(-32.98, -74.25) * mm, "end": v(-14.98, -92.25) * mm});
            skLineSegment(sketch, "E88.MirrorCS", {"start": v(-14.98, -92.25) * mm, "end": v(-14.98, -103.41) * mm});
            skArc(sketch, "E89.MirrorCS", {"start": v(15, -104.25) * mm, "mid": v(-0.42, -119.24) * mm, "end": v(-14.98, -103.41) * mm});
            skLineSegment(sketch, "E90.MirrorCS", {"start": v(15, -104.25) * mm, "end": v(15, -92.25) * mm});
            skLineSegment(sketch, "E91.MirrorCS", {"start": v(15, -92.25) * mm, "end": v(33, -74.25) * mm});
            skCircle(sketch, "E92.MirrorC", {"center": v(0, -104.25) * mm, "radius": 6 * mm});
            skLineSegment(sketch, "E93.MirrorCS", {"start": v(0, -74.25) * mm, "end": v(0, -104.25) * mm, "construction": true});
            skSolve(sketch);
        }
        {
            var Q0;
            Q0=makeQuery(id+"F16.imprint","IMPRINT",FACE,{"disambiguationData":[TD([[makeQuery(id+"F16.imprint","IMPRINT",EDGE,{"derivedFrom":makeQuery(id+"F1.opExtrude","CAP_EDGE",EDGE,{"disambiguationData":[OSD([sQuery(id+"F0.wireOp",EDGE,"E1.left")])],"isStart":true})}),-1.0]])]});
            var Q1;
            {var subQ0=sQuery(id+"F16.wireOp",EDGE,"E87.MirrorCS");Q1=makeQuery(id+"F16.imprint","IMPRINT",FACE,{"disambiguationData":[TD([[makeQuery(id+"F16.imprint","IMPRINT",EDGE,{"derivedFrom":subQ0}),1.0]])]});}
            var Q2;
            {var subQ0=sQuery(id+"F16.wireOp",EDGE,"E80");Q2=makeQuery(id+"F16.imprint","IMPRINT",FACE,{"disambiguationData":[TD([[makeQuery(id+"F16.imprint","IMPRINT",EDGE,{"derivedFrom":subQ0}),-1.0]])]});}
            var Q3;
            Q3=makeQuery(id+"F2.opExtrude","CAP_FACE",FACE,{"disambiguationData":[OSD([sQuery(id+"F0.wireOp",EDGE,"E12"),sQuery(id+"F0.wireOp",EDGE,"E13"),sQuery(id+"F0.wireOp",EDGE,"E14"),sQuery(id+"F0.wireOp",EDGE,"E15"),sQuery(id+"F0.wireOp",EDGE,"E17.filletArc"),sQuery(id+"F0.wireOp",EDGE,"E18.filletArc"),sQuery(id+"F0.wireOp",EDGE,"E19.filletArc"),sQuery(id+"F0.wireOp",EDGE,"E20.filletArc"),sQuery(id+"F0.wireOp",EDGE,"E25.0"),sQuery(id+"F0.wireOp",EDGE,"E25.1"),sQuery(id+"F0.wireOp",EDGE,"E25.2"),sQuery(id+"F0.wireOp",EDGE,"E25.3"),sQuery(id+"F0.wireOp",EDGE,"E25.4"),sQuery(id+"F0.wireOp",EDGE,"E25.5"),sQuery(id+"F0.wireOp",EDGE,"E25.6"),sQuery(id+"F0.wireOp",EDGE,"E25.7")])],"isStart":false});
            extrude(context, id + "F17", {"entities" : qUnion([Q0, Q1, Q2]), "operationType" : NewBodyOperationType.ADD, "endBound" : BoundingType.UP_TO_SURFACE, "endBoundEntityFace" : qUnion([Q3]), "depth" : 25 * mm});
        }
    });
